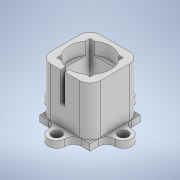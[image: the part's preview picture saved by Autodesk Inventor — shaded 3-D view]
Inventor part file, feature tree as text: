
AUTODESK INVENTOR PART (.ipt)
format: ipt  version: 2022 (Build 260153000, 153)  size: 361,472 bytes
history: native  units: in
note: dims shown in document units (in); Inventor stores cm internally (conversion verified against a paired STEP export)
features: projected_geometry x12, extrude x9, sketch x9, chamfer x2, fillet x2
ambient origin geometry x8: Origin, YZ Plane, XZ Plane, XY Plane, X Axis, Y Axis, Z Axis, Center Point
bodies: Solid1 (feature_tree)
feature tree (34):
  extrude  "Extrusion1"  Depth=0.3986in
  extrude  "Extrusion2"  Depth=0.1in
  extrude  "Extrusion3"  Depth=0.1in
  extrude  "Extrusion4"  Depth=0.05in
  extrude  "Extrusion5"  Depth=0.0787in TaperAngle=0.0deg
  chamfer  "Chamfer4"  Distance=0.0787in
  chamfer  "Chamfer5"  Angle=90.0deg  [1 undecoded]
  extrude  "Extrusion6"  TaperAngle=90.0deg  [1 undecoded]
  fillet  "Fillet2"  Radius=0.75in
  extrude  "Extrusion7"  Depth=0.0787in TaperAngle=0.0deg
  fillet  "Fillet3"  Radius=0.125in
  extrude  "Extrusion8"  Depth=0.125in TaperAngle=45.0deg
  extrude  "Extrusion9"  Depth=0.1in
  sketch  "Sketch1"  dims[d0=0.3986in d1=0.3986in]
  sketch  "Sketch2"  dims[d2=0.1in d3=0.1in]
  projected_geometry  "Projected Loop1"
  sketch  "Sketch3"  dims[d4=0.1in d5=0.1in]
  sketch  "Sketch4"  dims[d6=0.315in d7=0.0in d8=0.05in]
  projected_geometry  "Projected Loop2"
  projected_geometry  "Projected Loop3"
  projected_geometry  "Projected Loop4"
  sketch  "Sketch5"  dims[d9=0.4331in d10=0.0in d11=0.0787in d12=0.0in]
  projected_geometry  "Projected Loop5"
  projected_geometry  "Projected Loop6"
  sketch  "Sketch6"  dims[d15=0.1in]
  projected_geometry  "Projected Loop7"
  sketch  "Sketch7"  dims[d16=0.1in]
  projected_geometry  "Projected Loop8"
  sketch  "Sketch8"  dims[d17=90.0deg]
  projected_geometry  "Projected Loop9"
  projected_geometry  "Projected Loop10"
  sketch  "Sketch9"  dims[d18=90.0deg d19=0.0787in d20=0.0in d31=90.0deg d32=90.0deg d33=0.75in d34=0.0787in d35=0.0in d36=0.1239in d37=0.125in d38=45.0deg d39=0.121in d40=0.125in d41=45.0deg d42=0.1in d43=0.2in d44=0.1in d45=0.2in d46=0.1in d47=0.1181in d48=0.1in d49=0.1181in d50=0.0787in d51=0.0in d52=0.1in d53=0.2in d54=0.1in d55=0.1in d56=0.2in d57=0.1in d58=0.1in d59=0.1181in d60=0.1181in d61=0.025in d62=0.0787in d63=0.0in d64=0.125in d65=0.4921in d66=0.1in d67=0.15in d68=0.0in d69=0.0in d70=0.1in d71=0.0in]
  projected_geometry  "Projected Loop11"
  projected_geometry  "Projected Loop12"
note: 2 required parameter values undecoded (feature->parameter linkage not recoverable at this tier; creation-order binding heuristic only, values carry confidence <= 0.55)
